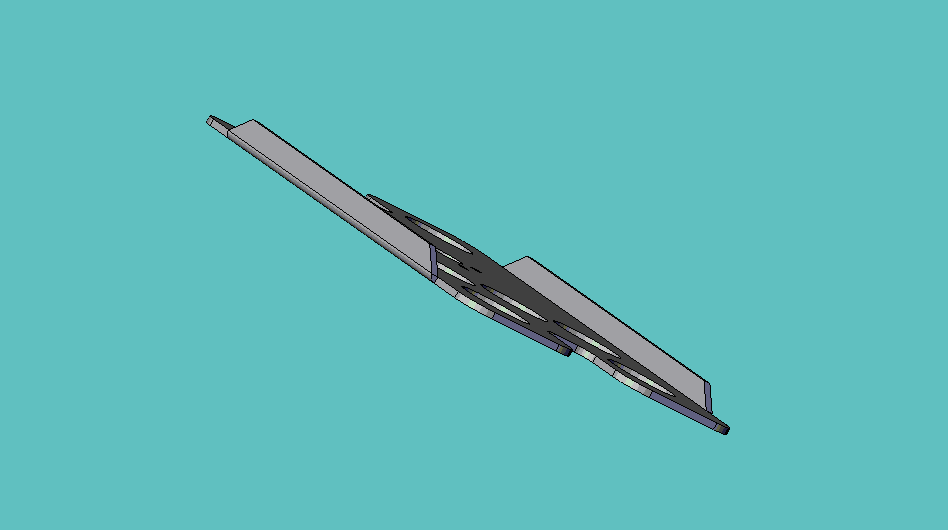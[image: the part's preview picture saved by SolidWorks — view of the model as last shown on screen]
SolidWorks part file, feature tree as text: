
SOLIDWORKS PART (.sldprt)
format: sldprt  version: not decoded by parser v0  size: 330,752 bytes
history: native  units: mm
features: sketch x3, extrude x2, material x1, cut_extrude x1, fillet x1 (+12 scaffold rows collapsed)
feature tree (20):
  scaffold x12  (default folders/planes/origin — collapsed)
  material  "Material <not specified>"
  sketch  "Sketch1"  dims[c1.D1=6.35mm c1.D2=6.35mm c2.D1=111.9124mm]
  extrude  "Extrude1"  Depth=1.524mm
  extrude  "Extrude2"  [1 undecoded]
  sketch  "Sketch1<3>"  dims[D1=6.35mm]
  sketch  "Sketch2"  dims[D1=6.35mm]
  cut_extrude  "Cut-Extrude1"  [1 undecoded]
  fillet  "Fillet1"  Radius=1.5875mm
decode coverage: 5 of 7 modeling features carry decoded parameters
note: 2 parameter values undecoded
note: suppression state not decoded; provenance and decode notes live in map.json
